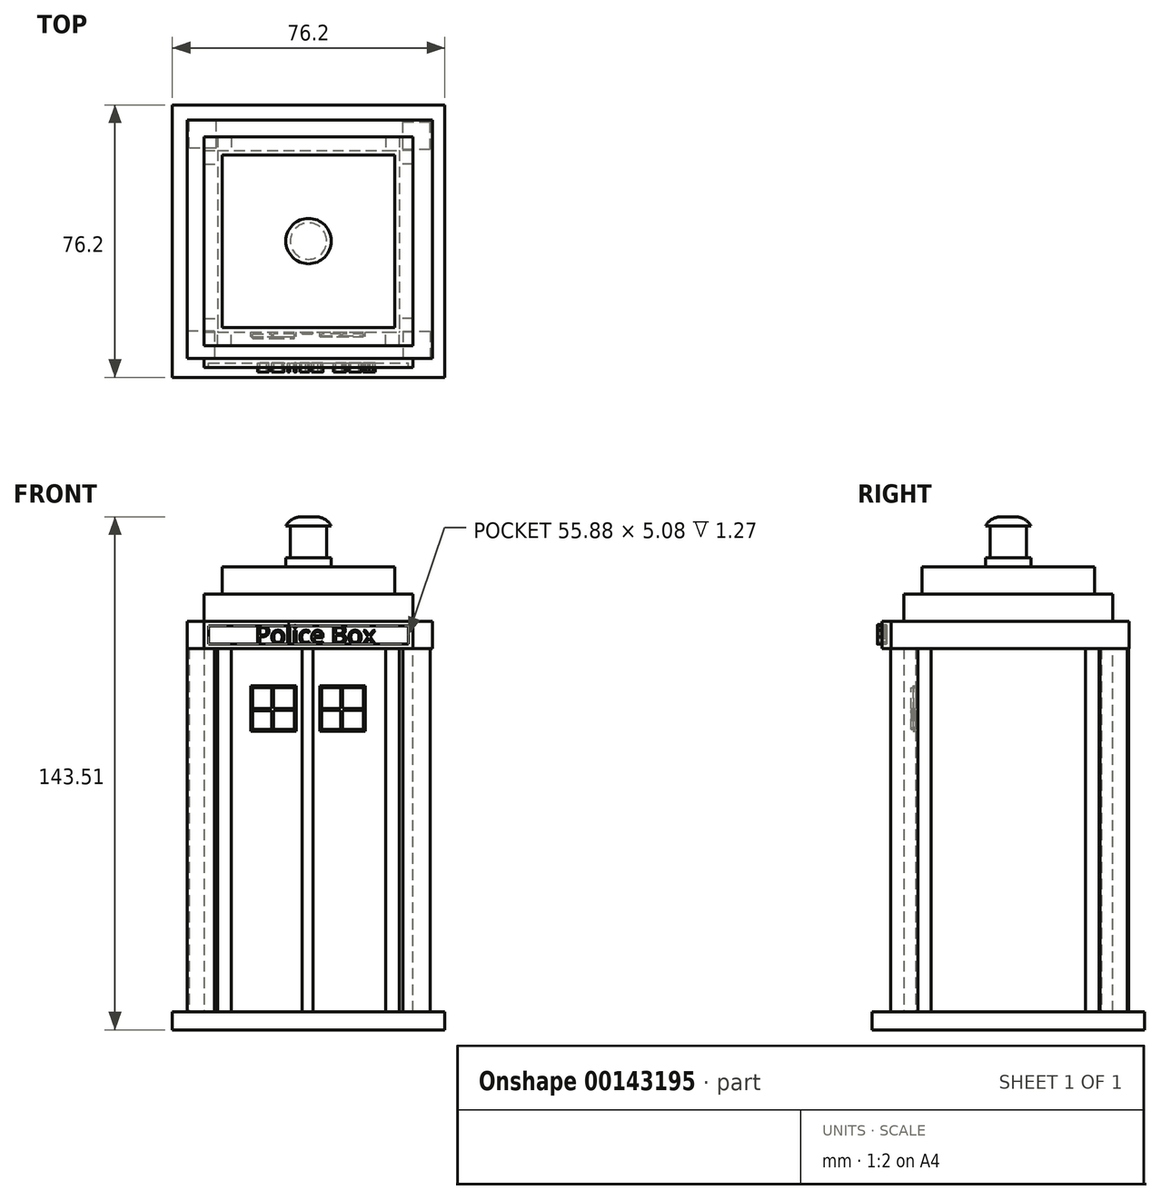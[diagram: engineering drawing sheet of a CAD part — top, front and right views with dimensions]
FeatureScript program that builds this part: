
annotation { "Feature Type Name" : "Feature", "Feature Type Description" : "" }
export const myFeature = defineFeature(function(context is Context, id is Id, definition is map)
    precondition{}
    {
        {
            var Q0;
            Q0=qCreatedBy(makeId("Front.planeOp"),FACE);
            var sketch = newSketch(context, id + "F0", { "sketchPlane" : qUnion([Q0])});
            skLineSegment(sketch, "E0.bottom", {"start": v(-38.1, 2.54) * mm, "end": v(38.1, 2.54) * mm});
            skLineSegment(sketch, "E0.top", {"start": v(-38.1, -2.54) * mm, "end": v(38.1, -2.54) * mm});
            skLineSegment(sketch, "E0.left", {"start": v(-38.1, 2.54) * mm, "end": v(-38.1, -2.54) * mm});
            skLineSegment(sketch, "E0.right", {"start": v(38.1, 2.54) * mm, "end": v(38.1, -2.54) * mm});
            skPoint(sketch, "E0.middle", {"position": v(0, 0) * mm});
            skSolve(sketch);
        }
        {
            var Q0;
            Q0 = qSketchRegion(id + "F0", true);
            extrude(context, id + "F1", {"entities" : qUnion([Q0]), "depth" : 38.1 * mm, "hasSecondDirection" : true, "secondDirectionOppositeDirection" : true, "secondDirectionDepth" : 38.1 * mm});
        }
        {
            var Q0;
            Q0=makeQuery(id+"F1.opExtrude","SWEPT_FACE",FACE,{"disambiguationData":[OSD([sQuery(id+"F0.wireOp",EDGE,"E0.bottom")])]});
            var sketch = newSketch(context, id + "F2", { "sketchPlane" : qUnion([Q0])});
            skLineSegment(sketch, "E1.bottom", {"start": v(-25.4, 25.4) * mm, "end": v(25.4, 25.4) * mm});
            skLineSegment(sketch, "E1.top", {"start": v(-25.4, -25.4) * mm, "end": v(25.4, -25.4) * mm});
            skLineSegment(sketch, "E1.left", {"start": v(-25.4, 25.4) * mm, "end": v(-25.4, -25.4) * mm});
            skLineSegment(sketch, "E1.right", {"start": v(25.4, 25.4) * mm, "end": v(25.4, -25.4) * mm});
            skPoint(sketch, "E1.middle", {"position": v(0, 0) * mm});
            skSolve(sketch);
        }
        {
            var Q0;
            Q0=makeQuery(id+"F2.imprint","IMPRINT",FACE,{"disambiguationData":[TD([[makeQuery(id+"F2.imprint","IMPRINT",EDGE,{"derivedFrom":sQuery(id+"F2.wireOp",EDGE,"E1.bottom")}),-1.0]])]});
            extrude(context, id + "F3", {"entities" : qUnion([Q0]), "depth" : 101.6 * mm});
        }
        {
            var Q0;
            Q0=makeQuery(id+"F1.opExtrude","SWEPT_FACE",FACE,{"disambiguationData":[OSD([sQuery(id+"F0.wireOp",EDGE,"E0.bottom")])]});
            var sketch = newSketch(context, id + "F4", { "sketchPlane" : qUnion([Q0])});
            skLineSegment(sketch, "E2.bottom", {"start": v(-22.25, 22.42) * mm, "end": v(-31.41, 22.42) * mm});
            skLineSegment(sketch, "E2.top", {"start": v(-22.25, 31.25) * mm, "end": v(-31.41, 31.25) * mm});
            skLineSegment(sketch, "E2.left", {"start": v(-22.25, 22.42) * mm, "end": v(-22.25, 31.25) * mm});
            skLineSegment(sketch, "E2.right", {"start": v(-31.41, 22.42) * mm, "end": v(-31.41, 31.25) * mm});
            skSolve(sketch);
        }
        {
            var Q0;
            Q0=makeQuery(id+"F4.imprint","IMPRINT",FACE,{"disambiguationData":[TD([[makeQuery(id+"F4.imprint","IMPRINT",EDGE,{"derivedFrom":sQuery(id+"F4.wireOp",EDGE,"E2.bottom")}),1.0]])]});
            var sketch = newSketch(context, id + "F5", { "sketchPlane" : qUnion([Q0])});
            skLineSegment(sketch, "E3.bottom", {"start": v(-26.3, -25.15) * mm, "end": v(-33.93, -25.15) * mm});
            skLineSegment(sketch, "E3.top", {"start": v(-26.3, -32.77) * mm, "end": v(-33.93, -32.77) * mm});
            skLineSegment(sketch, "E3.left", {"start": v(-26.3, -25.15) * mm, "end": v(-26.3, -32.77) * mm});
            skLineSegment(sketch, "E3.right", {"start": v(-33.93, -25.15) * mm, "end": v(-33.93, -32.77) * mm});
            skLineSegment(sketch, "E4.bottom", {"start": v(26.41, 25.69) * mm, "end": v(34.03, 25.69) * mm});
            skLineSegment(sketch, "E4.top", {"start": v(26.41, 33.3) * mm, "end": v(34.03, 33.3) * mm});
            skLineSegment(sketch, "E4.left", {"start": v(26.41, 25.69) * mm, "end": v(26.41, 33.3) * mm});
            skLineSegment(sketch, "E4.right", {"start": v(34.03, 25.69) * mm, "end": v(34.03, 33.3) * mm});
            skLineSegment(sketch, "E5.bottom", {"start": v(26.41, -25.27) * mm, "end": v(34.03, -25.27) * mm});
            skLineSegment(sketch, "E5.top", {"start": v(26.41, -32.89) * mm, "end": v(34.03, -32.89) * mm});
            skLineSegment(sketch, "E5.left", {"start": v(26.41, -25.27) * mm, "end": v(26.41, -32.89) * mm});
            skLineSegment(sketch, "E5.right", {"start": v(34.03, -25.27) * mm, "end": v(34.03, -32.89) * mm});
            skLineSegment(sketch, "E6.bottom", {"start": v(-25.76, 26.02) * mm, "end": v(-33.38, 26.02) * mm});
            skLineSegment(sketch, "E6.top", {"start": v(-25.76, 33.64) * mm, "end": v(-33.38, 33.64) * mm});
            skLineSegment(sketch, "E6.left", {"start": v(-25.76, 26.02) * mm, "end": v(-25.76, 33.64) * mm});
            skLineSegment(sketch, "E6.right", {"start": v(-33.38, 26.02) * mm, "end": v(-33.38, 33.64) * mm});
            skSolve(sketch);
        }
        {
            var Q0;
            Q0 = qSketchRegion(id + "F5", true);
            extrude(context, id + "F6", {"entities" : qUnion([Q0]), "depth" : 101.6 * mm});
        }
        {
            var Q0;
            Q0=makeQuery(id+"F3.opExtrude","SWEPT_FACE",FACE,{"disambiguationData":[OSD([sQuery(id+"F2.wireOp",EDGE,"E1.bottom")])]});
            var sketch = newSketch(context, id + "F7", { "sketchPlane" : qUnion([Q0])});
            skLineSegment(sketch, "E7.bottom", {"start": v(-25.4, 104.14) * mm, "end": v(-19.36, 104.14) * mm});
            skLineSegment(sketch, "E7.top", {"start": v(-25.4, 2.54) * mm, "end": v(-19.36, 2.54) * mm});
            skLineSegment(sketch, "E7.left", {"start": v(-25.4, 104.14) * mm, "end": v(-25.4, 2.54) * mm});
            skLineSegment(sketch, "E8.bottom", {"start": v(25.4, 104.14) * mm, "end": v(21.59, 104.14) * mm});
            skLineSegment(sketch, "E8.top", {"start": v(25.4, 2.54) * mm, "end": v(21.6, 2.54) * mm});
            skLineSegment(sketch, "E8.left", {"start": v(25.4, 104.14) * mm, "end": v(25.4, 2.54) * mm});
            skLineSegment(sketch, "E8.right", {"start": v(21.59, 104.14) * mm, "end": v(21.6, 2.54) * mm});
            skLineSegment(sketch, "E9.bottom", {"start": v(-25.4, 2.54) * mm, "end": v(-21.59, 2.54) * mm});
            skLineSegment(sketch, "E9.top", {"start": v(-25.4, 104.14) * mm, "end": v(-21.6, 104.14) * mm});
            skLineSegment(sketch, "E9.left", {"start": v(-25.4, 2.54) * mm, "end": v(-25.4, 104.14) * mm});
            skLineSegment(sketch, "E9.right", {"start": v(-21.59, 2.54) * mm, "end": v(-21.6, 104.14) * mm});
            skSolve(sketch);
        }
        {
            var Q0;
            Q0 = qSketchRegion(id + "F7", true);
            extrude(context, id + "F8", {"entities" : qUnion([Q0]), "depth" : 3.8 * mm});
        }
        {
            var Q0;
            Q0=makeQuery(id+"F3.opExtrude","SWEPT_FACE",FACE,{"disambiguationData":[OSD([sQuery(id+"F2.wireOp",EDGE,"E1.right")])]});
            var sketch = newSketch(context, id + "F9", { "sketchPlane" : qUnion([Q0])});
            skLineSegment(sketch, "E10.bottom", {"start": v(-25.4, 2.54) * mm, "end": v(-21.6, 2.54) * mm});
            skLineSegment(sketch, "E10.top", {"start": v(-25.4, 104.14) * mm, "end": v(-21.6, 104.14) * mm});
            skLineSegment(sketch, "E10.left", {"start": v(-25.4, 2.54) * mm, "end": v(-25.4, 104.14) * mm});
            skLineSegment(sketch, "E10.right", {"start": v(-21.6, 2.54) * mm, "end": v(-21.6, 104.14) * mm});
            skLineSegment(sketch, "E11.bottom", {"start": v(25.4, 104.14) * mm, "end": v(21.59, 104.14) * mm});
            skLineSegment(sketch, "E11.top", {"start": v(25.4, 2.54) * mm, "end": v(21.6, 2.54) * mm});
            skLineSegment(sketch, "E11.left", {"start": v(25.4, 104.14) * mm, "end": v(25.4, 2.54) * mm});
            skLineSegment(sketch, "E11.right", {"start": v(21.59, 104.14) * mm, "end": v(21.6, 2.54) * mm});
            skSolve(sketch);
        }
        {
            var Q0;
            Q0 = qSketchRegion(id + "F9", true);
            extrude(context, id + "F10", {"entities" : qUnion([Q0]), "depth" : 3.8 * mm});
        }
        {
            var Q0;
            Q0=makeQuery(id+"F3.opExtrude","SWEPT_FACE",FACE,{"disambiguationData":[OSD([sQuery(id+"F2.wireOp",EDGE,"E1.top")])]});
            var sketch = newSketch(context, id + "F11", { "sketchPlane" : qUnion([Q0])});
            skLineSegment(sketch, "E12.bottom", {"start": v(-25.4, 104.14) * mm, "end": v(-21.6, 104.14) * mm});
            skLineSegment(sketch, "E12.top", {"start": v(-25.4, 2.54) * mm, "end": v(-21.59, 2.54) * mm});
            skLineSegment(sketch, "E12.left", {"start": v(-25.4, 104.14) * mm, "end": v(-25.4, 2.54) * mm});
            skLineSegment(sketch, "E12.right", {"start": v(-21.6, 104.14) * mm, "end": v(-21.59, 2.54) * mm});
            skLineSegment(sketch, "E13.bottom", {"start": v(25.4, 104.14) * mm, "end": v(21.59, 104.14) * mm});
            skLineSegment(sketch, "E13.top", {"start": v(25.4, 2.54) * mm, "end": v(21.6, 2.54) * mm});
            skLineSegment(sketch, "E13.left", {"start": v(25.4, 104.14) * mm, "end": v(25.4, 2.54) * mm});
            skLineSegment(sketch, "E13.right", {"start": v(21.59, 104.14) * mm, "end": v(21.6, 2.54) * mm});
            skSolve(sketch);
        }
        {
            var Q0;
            Q0 = qSketchRegion(id + "F11", true);
            extrude(context, id + "F12", {"entities" : qUnion([Q0]), "depth" : 3.8 * mm});
        }
        {
            var Q0;
            Q0=makeQuery(id+"F3.opExtrude","SWEPT_FACE",FACE,{"disambiguationData":[OSD([sQuery(id+"F2.wireOp",EDGE,"E1.left")])]});
            var sketch = newSketch(context, id + "F13", { "sketchPlane" : qUnion([Q0])});
            skLineSegment(sketch, "E14.bottom", {"start": v(-25.4, 104.14) * mm, "end": v(-21.59, 104.14) * mm});
            skLineSegment(sketch, "E14.top", {"start": v(-25.4, 2.54) * mm, "end": v(-21.59, 2.54) * mm});
            skLineSegment(sketch, "E14.left", {"start": v(-25.4, 104.14) * mm, "end": v(-25.4, 2.54) * mm});
            skLineSegment(sketch, "E14.right", {"start": v(-21.59, 104.14) * mm, "end": v(-21.59, 2.54) * mm});
            skLineSegment(sketch, "E15.bottom", {"start": v(25.4, 104.14) * mm, "end": v(21.59, 104.14) * mm});
            skLineSegment(sketch, "E15.top", {"start": v(25.4, 2.54) * mm, "end": v(21.6, 2.54) * mm});
            skLineSegment(sketch, "E15.left", {"start": v(25.4, 104.14) * mm, "end": v(25.4, 2.54) * mm});
            skLineSegment(sketch, "E15.right", {"start": v(21.59, 104.14) * mm, "end": v(21.6, 2.54) * mm});
            skSolve(sketch);
        }
        {
            var Q0;
            Q0 = qSketchRegion(id + "F13", true);
            extrude(context, id + "F14", {"entities" : qUnion([Q0]), "depth" : 3.8 * mm});
        }
        {
            var Q0;
            Q0=makeQuery(id+"F3.opExtrude","SWEPT_FACE",FACE,{"disambiguationData":[OSD([sQuery(id+"F2.wireOp",EDGE,"E1.top")])]});
            var sketch = newSketch(context, id + "F15", { "sketchPlane" : qUnion([Q0])});
            skLineSegment(sketch, "E16.bottom", {"start": v(-16.15, 93.64) * mm, "end": v(-3.45, 93.64) * mm});
            skLineSegment(sketch, "E16.top", {"start": v(-16.15, 80.94) * mm, "end": v(-3.45, 80.94) * mm});
            skLineSegment(sketch, "E16.left", {"start": v(-16.15, 93.64) * mm, "end": v(-16.15, 80.94) * mm});
            skLineSegment(sketch, "E16.right", {"start": v(-3.45, 93.64) * mm, "end": v(-3.45, 80.94) * mm});
            skPoint(sketch, "E16.middle", {"position": v(-9.8, 87.3) * mm});
            skLineSegment(sketch, "E17.bottom", {"start": v(3.2, 93.64) * mm, "end": v(15.9, 93.64) * mm});
            skLineSegment(sketch, "E17.top", {"start": v(3.2, 80.94) * mm, "end": v(15.9, 80.94) * mm});
            skLineSegment(sketch, "E17.left", {"start": v(3.2, 93.64) * mm, "end": v(3.2, 80.94) * mm});
            skLineSegment(sketch, "E17.right", {"start": v(15.9, 93.64) * mm, "end": v(15.9, 80.94) * mm});
            skPoint(sketch, "E17.middle", {"position": v(9.55, 87.3) * mm});
            skPoint(sketch, "E17.middle.positionSnap0", {"position": v(-3.45, 87.3) * mm});
            skPoint(sketch, "E17.centerSnap0", {"position": v(-3.45, 87.3) * mm});
            skSolve(sketch);
        }
        {
            var Q0;
            Q0 = qSketchRegion(id + "F15", true);
            extrude(context, id + "F16", {"entities" : qUnion([Q0]), "depth" : 1.27 * mm});
        }
        {
            var Q0;
            Q0=makeQuery(id+"F16.opExtrude","CAP_FACE",FACE,{"disambiguationData":[OSD([sQuery(id+"F15.wireOp",EDGE,"E16.bottom"),sQuery(id+"F15.wireOp",EDGE,"E16.top"),sQuery(id+"F15.wireOp",EDGE,"E16.left"),sQuery(id+"F15.wireOp",EDGE,"E16.right")])],"isStart":false});
            var Q1;
            Q1=makeQuery(id+"F16.opExtrude","CAP_FACE",FACE,{"disambiguationData":[OSD([sQuery(id+"F15.wireOp",EDGE,"E17.bottom"),sQuery(id+"F15.wireOp",EDGE,"E17.top"),sQuery(id+"F15.wireOp",EDGE,"E17.left"),sQuery(id+"F15.wireOp",EDGE,"E17.right")])],"isStart":false});
            shell(context, id + "F17", {"entities" : qUnion([Q0, Q1]), "thickness" : 0.5 * mm});
        }
        {
            var Q0;
            Q0=makeQuery(id+"F17.opShell","OFFSET_FACE",FACE,{"disambiguationData":[OSD([sQuery(id+"F15.wireOp",EDGE,"E16.bottom"),sQuery(id+"F15.wireOp",EDGE,"E16.top"),sQuery(id+"F15.wireOp",EDGE,"E16.left"),sQuery(id+"F15.wireOp",EDGE,"E16.right")])]});
            var sketch = newSketch(context, id + "F18", { "sketchPlane" : qUnion([Q0])});
            skLineSegment(sketch, "E18", {"start": v(-10.35, 93.14) * mm, "end": v(-10.35, 81.45) * mm});
            skLineSegment(sketch, "E19", {"start": v(-10.35, 81.45) * mm, "end": v(-9.8, 81.45) * mm});
            skLineSegment(sketch, "E20", {"start": v(-9.8, 81.45) * mm, "end": v(-9.8, 93.14) * mm});
            skLineSegment(sketch, "E21", {"start": v(-9.8, 93.14) * mm, "end": v(-10.35, 93.14) * mm});
            skLineSegment(sketch, "E22", {"start": v(-3.96, 87.3) * mm, "end": v(-9.8, 87.3) * mm});
            skLineSegment(sketch, "E23", {"start": v(-9.8, 87.3) * mm, "end": v(-9.8, 86.77) * mm});
            skLineSegment(sketch, "E24", {"start": v(-9.8, 86.77) * mm, "end": v(-3.96, 86.77) * mm});
            skLineSegment(sketch, "E25", {"start": v(-3.96, 86.77) * mm, "end": v(-3.96, 87.3) * mm});
            skLineSegment(sketch, "E26", {"start": v(-15.65, 87.3) * mm, "end": v(-10.35, 87.3) * mm});
            skLineSegment(sketch, "E27", {"start": v(-10.35, 87.3) * mm, "end": v(-10.35, 86.72) * mm});
            skLineSegment(sketch, "E28", {"start": v(-10.35, 86.72) * mm, "end": v(-15.65, 86.72) * mm});
            skLineSegment(sketch, "E29", {"start": v(-15.65, 86.72) * mm, "end": v(-15.65, 87.3) * mm});
            skSolve(sketch);
        }
        {
            var Q0;
            Q0 = qSketchRegion(id + "F18", true);
            extrude(context, id + "F19", {"entities" : qUnion([Q0]), "operationType" : NewBodyOperationType.ADD, "depth" : 1.27 * mm});
        }
        {
            var Q0;
            Q0=makeQuery(id+"F17.opShell","OFFSET_FACE",FACE,{"disambiguationData":[OSD([sQuery(id+"F15.wireOp",EDGE,"E17.bottom"),sQuery(id+"F15.wireOp",EDGE,"E17.top"),sQuery(id+"F15.wireOp",EDGE,"E17.left"),sQuery(id+"F15.wireOp",EDGE,"E17.right")])]});
            var sketch = newSketch(context, id + "F20", { "sketchPlane" : qUnion([Q0])});
            skLineSegment(sketch, "E30", {"start": v(9.05, 93.14) * mm, "end": v(9.05, 81.45) * mm});
            skLineSegment(sketch, "E31", {"start": v(9.05, 81.45) * mm, "end": v(9.55, 81.45) * mm});
            skLineSegment(sketch, "E32", {"start": v(9.55, 81.45) * mm, "end": v(9.55, 93.14) * mm});
            skLineSegment(sketch, "E33", {"start": v(9.55, 93.14) * mm, "end": v(9.05, 93.14) * mm});
            skLineSegment(sketch, "E34", {"start": v(15.4, 87.3) * mm, "end": v(9.55, 87.3) * mm});
            skLineSegment(sketch, "E35", {"start": v(9.55, 87.3) * mm, "end": v(9.55, 86.8) * mm});
            skLineSegment(sketch, "E36", {"start": v(9.55, 86.8) * mm, "end": v(15.4, 86.8) * mm});
            skLineSegment(sketch, "E37", {"start": v(15.4, 86.8) * mm, "end": v(15.4, 87.3) * mm});
            skLineSegment(sketch, "E38", {"start": v(9.05, 87.3) * mm, "end": v(3.7, 87.3) * mm});
            skLineSegment(sketch, "E39", {"start": v(3.7, 87.3) * mm, "end": v(3.7, 86.8) * mm});
            skLineSegment(sketch, "E40", {"start": v(3.7, 86.8) * mm, "end": v(9.05, 86.8) * mm});
            skLineSegment(sketch, "E41", {"start": v(9.05, 86.8) * mm, "end": v(9.05, 87.3) * mm});
            skSolve(sketch);
        }
        {
            var Q0;
            Q0 = qSketchRegion(id + "F20", true);
            extrude(context, id + "F21", {"entities" : qUnion([Q0]), "operationType" : NewBodyOperationType.ADD, "depth" : 0.5 * mm});
        }
        {
            var Q0;
            Q0=makeQuery(id+"F3.opExtrude","SWEPT_FACE",FACE,{"disambiguationData":[OSD([sQuery(id+"F2.wireOp",EDGE,"E1.top")])]});
            var sketch = newSketch(context, id + "F22", { "sketchPlane" : qUnion([Q0])});
            skLineSegment(sketch, "E42", {"start": v(-1.83, 104.14) * mm, "end": v(-1.83, 2.54) * mm});
            skLineSegment(sketch, "E43", {"start": v(-1.83, 2.54) * mm, "end": v(1.22, 2.54) * mm});
            skLineSegment(sketch, "E44", {"start": v(1.22, 2.54) * mm, "end": v(1.22, 104.14) * mm});
            skLineSegment(sketch, "E45", {"start": v(1.22, 104.14) * mm, "end": v(-1.83, 104.14) * mm});
            skSolve(sketch);
        }
        {
            var Q0;
            Q0 = qSketchRegion(id + "F22", true);
            extrude(context, id + "F23", {"entities" : qUnion([Q0]), "depth" : 0.5 * mm});
        }
        {
            var Q0;
            Q0=makeQuery(id+"F6.opExtrude","CAP_FACE",FACE,{"disambiguationData":[OSD([sQuery(id+"F5.wireOp",EDGE,"E3.bottom"),sQuery(id+"F5.wireOp",EDGE,"E3.top"),sQuery(id+"F5.wireOp",EDGE,"E3.left"),sQuery(id+"F5.wireOp",EDGE,"E3.right")])],"isStart":false});
            var sketch = newSketch(context, id + "F24", { "sketchPlane" : qUnion([Q0])});
            skLineSegment(sketch, "E46.bottom", {"start": v(-33.93, -32.77) * mm, "end": v(34.65, -32.77) * mm});
            skLineSegment(sketch, "E46.top", {"start": v(-33.93, 33.88) * mm, "end": v(34.65, 33.88) * mm});
            skLineSegment(sketch, "E46.left", {"start": v(-33.93, -32.77) * mm, "end": v(-33.93, 33.88) * mm});
            skLineSegment(sketch, "E46.right", {"start": v(34.65, -32.77) * mm, "end": v(34.65, 33.88) * mm});
            skSolve(sketch);
        }
        {
            var Q0;
            Q0 = qSketchRegion(id + "F24", true);
            extrude(context, id + "F25", {"entities" : qUnion([Q0]), "depth" : 7.62 * mm});
        }
        {
            var Q0;
            Q0=makeQuery(id+"F25.opExtrude","CAP_FACE",FACE,{"disambiguationData":[OSD([sQuery(id+"F24.wireOp",EDGE,"E46.bottom"),sQuery(id+"F24.wireOp",EDGE,"E46.top"),sQuery(id+"F24.wireOp",EDGE,"E46.left"),sQuery(id+"F24.wireOp",EDGE,"E46.right")])],"isStart":false});
            var sketch = newSketch(context, id + "F26", { "sketchPlane" : qUnion([Q0])});
            skLineSegment(sketch, "E47.bottom", {"start": v(-29.2, 29.21) * mm, "end": v(29.21, 29.21) * mm});
            skLineSegment(sketch, "E47.top", {"start": v(-29.21, -29.21) * mm, "end": v(29.2, -29.21) * mm});
            skLineSegment(sketch, "E47.left", {"start": v(-29.2, 29.21) * mm, "end": v(-29.21, -29.21) * mm});
            skLineSegment(sketch, "E47.right", {"start": v(29.21, 29.21) * mm, "end": v(29.2, -29.21) * mm});
            skPoint(sketch, "E47.middle", {"position": v(0, 0) * mm});
            skSolve(sketch);
        }
        {
            var Q0;
            Q0 = qSketchRegion(id + "F26", true);
            extrude(context, id + "F27", {"entities" : qUnion([Q0]), "operationType" : NewBodyOperationType.ADD, "depth" : 7.62 * mm});
        }
        {
            var Q0;
            Q0=makeQuery(id+"F27.opExtrude","CAP_FACE",FACE,{"disambiguationData":[OSD([sQuery(id+"F26.wireOp",EDGE,"E47.bottom"),sQuery(id+"F26.wireOp",EDGE,"E47.top"),sQuery(id+"F26.wireOp",EDGE,"E47.left"),sQuery(id+"F26.wireOp",EDGE,"E47.right")])],"isStart":false});
            var sketch = newSketch(context, id + "F28", { "sketchPlane" : qUnion([Q0])});
            skLineSegment(sketch, "E48.bottom", {"start": v(-24.13, 24.13) * mm, "end": v(24.13, 24.13) * mm});
            skLineSegment(sketch, "E48.top", {"start": v(-24.13, -24.13) * mm, "end": v(24.13, -24.13) * mm});
            skLineSegment(sketch, "E48.left", {"start": v(-24.13, 24.13) * mm, "end": v(-24.13, -24.13) * mm});
            skLineSegment(sketch, "E48.right", {"start": v(24.13, 24.13) * mm, "end": v(24.13, -24.13) * mm});
            skPoint(sketch, "E48.middle", {"position": v(0, 0) * mm});
            skSolve(sketch);
        }
        {
            var Q0;
            Q0 = qSketchRegion(id + "F28", true);
            extrude(context, id + "F29", {"entities" : qUnion([Q0]), "operationType" : NewBodyOperationType.ADD, "depth" : 7.62 * mm});
        }
        {
            var Q0;
            Q0=makeQuery(id+"F29.opExtrude","CAP_FACE",FACE,{"disambiguationData":[OSD([sQuery(id+"F28.wireOp",EDGE,"E48.bottom"),sQuery(id+"F28.wireOp",EDGE,"E48.top"),sQuery(id+"F28.wireOp",EDGE,"E48.left"),sQuery(id+"F28.wireOp",EDGE,"E48.right")])],"isStart":false});
            var sketch = newSketch(context, id + "F30", { "sketchPlane" : qUnion([Q0])});
            skCircle(sketch, "E49", {"center": v(0, 0) * mm, "radius": 6.35 * mm});
            skSolve(sketch);
        }
        {
            var Q0;
            Q0 = qSketchRegion(id + "F30", true);
            extrude(context, id + "F31", {"entities" : qUnion([Q0]), "operationType" : NewBodyOperationType.ADD, "depth" : 2.54 * mm});
        }
        {
            var Q0;
            Q0=makeQuery(id+"F31.opExtrude","CAP_FACE",FACE,{"disambiguationData":[OSD([sQuery(id+"F30.wireOp",EDGE,"E49")])],"isStart":false});
            var sketch = newSketch(context, id + "F32", { "sketchPlane" : qUnion([Q0])});
            skCircle(sketch, "E50", {"center": v(0, 0) * mm, "radius": 5.08 * mm});
            skSolve(sketch);
        }
        {
            var Q0;
            Q0 = qSketchRegion(id + "F32", true);
            extrude(context, id + "F33", {"entities" : qUnion([Q0]), "depth" : 8.9 * mm});
        }
        {
            var Q0;
            Q0=makeQuery(id+"F33.opExtrude","CAP_FACE",FACE,{"disambiguationData":[OSD([sQuery(id+"F32.wireOp",EDGE,"E50")])],"isStart":false});
            var sketch = newSketch(context, id + "F34", { "sketchPlane" : qUnion([Q0])});
            skCircle(sketch, "E51", {"center": v(0, 0) * mm, "radius": 6.35 * mm});
            skSolve(sketch);
        }
        {
            var Q0;
            Q0 = qSketchRegion(id + "F34", true);
            extrude(context, id + "F35", {"entities" : qUnion([Q0]), "depth" : 2.54 * mm});
        }
        {
            var Q0;
            Q0=makeQuery(id+"F35.opExtrude","CAP_EDGE",EDGE,{"disambiguationData":[OSD([sQuery(id+"F34.wireOp",EDGE,"E51")])],"isStart":false});
            fillet(context, id + "F36", {"entities" : qUnion([Q0]), "radius" : 5.08 * mm, "tangentPropagation" : true, "allowEdgeOverflow" : false});
        }
        {
            var Q0;
            Q0=makeQuery(id+"F25.opExtrude","SWEPT_FACE",FACE,{"disambiguationData":[OSD([sQuery(id+"F24.wireOp",EDGE,"E46.bottom")])]});
            var sketch = newSketch(context, id + "F37", { "sketchPlane" : qUnion([Q0])});
            skLineSegment(sketch, "E52.bottom", {"start": v(-29.21, 111.76) * mm, "end": v(29.21, 111.76) * mm});
            skLineSegment(sketch, "E52.top", {"start": v(-29.21, 104.14) * mm, "end": v(29.21, 104.14) * mm});
            skLineSegment(sketch, "E52.left", {"start": v(-29.21, 111.76) * mm, "end": v(-29.21, 104.14) * mm});
            skLineSegment(sketch, "E52.right", {"start": v(29.21, 111.76) * mm, "end": v(29.21, 104.14) * mm});
            skPoint(sketch, "E52.middle", {"position": v(0, 107.95) * mm});
            skSolve(sketch);
        }
        {
            var Q0;
            Q0 = qSketchRegion(id + "F37", true);
            extrude(context, id + "F38", {"entities" : qUnion([Q0]), "depth" : 2.54 * mm});
        }
        {
            var Q0;
            Q0=makeQuery(id+"F38.opExtrude","CAP_FACE",FACE,{"disambiguationData":[OSD([sQuery(id+"F37.wireOp",EDGE,"E52.bottom"),sQuery(id+"F37.wireOp",EDGE,"E52.top"),sQuery(id+"F37.wireOp",EDGE,"E52.left"),sQuery(id+"F37.wireOp",EDGE,"E52.right")])],"isStart":false});
            shell(context, id + "F39", {"entities" : qUnion([Q0]), "thickness" : 1.27 * mm});
        }
        {
            var Q0;
            Q0=makeQuery(id+"F39.opShell","OFFSET_FACE",FACE,{"disambiguationData":[OSD([sQuery(id+"F37.wireOp",EDGE,"E52.bottom"),sQuery(id+"F37.wireOp",EDGE,"E52.top"),sQuery(id+"F37.wireOp",EDGE,"E52.left"),sQuery(id+"F37.wireOp",EDGE,"E52.right")])]});
            var sketch = newSketch(context, id + "F40", { "sketchPlane" : qUnion([Q0])});
            skText(sketch, "E53", { "text": "Police Box", "fontName": "OpenSans-Regular.ttf"});
            const initialGuessF40  = {"E53": [-0.01495, 0.10541, 1, 0, 0.00508]};
            skSetInitialGuess(sketch, initialGuessF40);
            skSolve(sketch);
        }
        {
            var Q0;
            Q0 = qSketchRegion(id + "F40", true);
            extrude(context, id + "F41", {"entities" : qUnion([Q0]), "depth" : 2.54 * mm});
        }
    });
